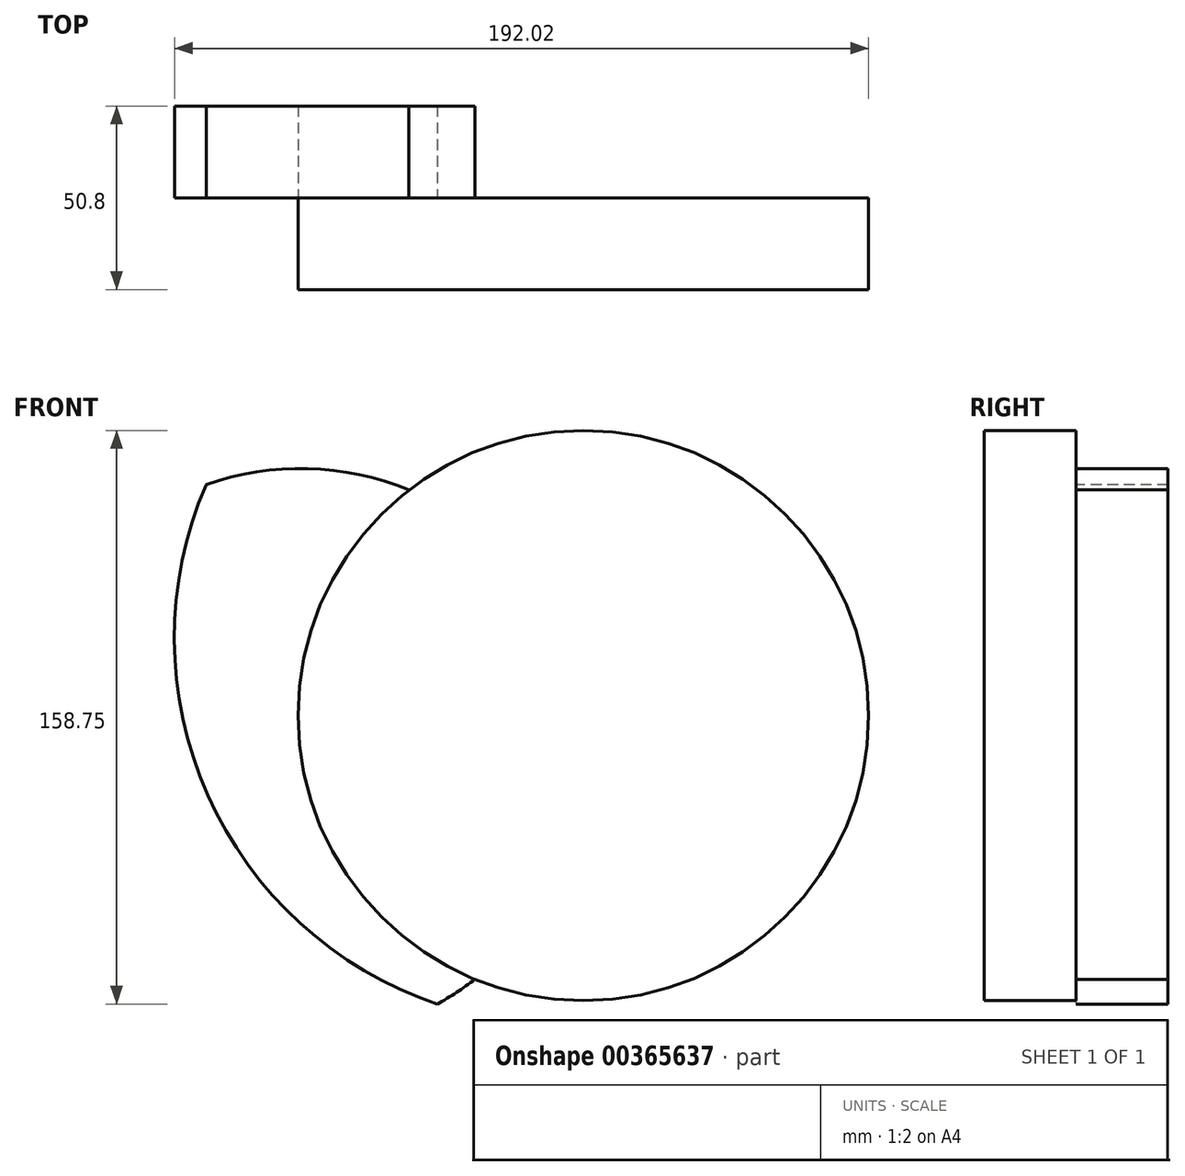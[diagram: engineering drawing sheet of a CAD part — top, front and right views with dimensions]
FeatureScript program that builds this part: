
annotation { "Feature Type Name" : "Feature", "Feature Type Description" : "" }
export const myFeature = defineFeature(function(context is Context, id is Id, definition is map)
    precondition{}
    {
        {
            var Q0;
            Q0=qCreatedBy(makeId("Front.planeOp"),FACE);
            var sketch = newSketch(context, id + "F0", { "sketchPlane" : qUnion([Q0])});
            skCircle(sketch, "E0", {"center": v(0, 0) * mm, "radius": 78.92 * mm});
            skSolve(sketch);
        }
        {
            var Q0;
            Q0=makeQuery(id+"F0.imprint","IMPRINT",FACE,{"disambiguationData":[TD([[makeQuery(id+"F0.imprint","IMPRINT",EDGE,{"derivedFrom":sQuery(id+"F0.wireOp",EDGE,"E0")}),1.0]])]});
            extrude(context, id + "F1", {"entities" : qUnion([Q0]), "depth" : 25.4 * mm});
        }
        {
            var Q0;
            Q0=makeQuery(id+"F1.opExtrude","CAP_FACE",FACE,{"disambiguationData":[OSD([sQuery(id+"F0.wireOp",EDGE,"E0")])],"isStart":true});
            var sketch = newSketch(context, id + "F2", { "sketchPlane" : qUnion([Q0])});
            skCircle(sketch, "E1", {"center": v(78.21, -10.54) * mm, "radius": 78.92 * mm});
            skCircle(sketch, "E2", {"center": v(6.1, 21.52) * mm, "radius": 107 * mm});
            skSolve(sketch);
        }
        {
            var Q0;
            {var subQ0=sQuery(id+"F2.wireOp",EDGE,"E1");var subQ1=makeQuery(id+"F1.opExtrude","CAP_EDGE",EDGE,{"disambiguationData":[OSD([sQuery(id+"F0.wireOp",EDGE,"E0")])],"isStart":true});var subQ2=makeQuery(id+"F2.imprint","INTERSECT",VERTEX,{"disambiguationData":[OD(0.0)],"derivedFrom":[subQ1,subQ0]});Q0=makeQuery(id+"F2.imprint","IMPRINT",FACE,{"disambiguationData":[TD([[makeQuery(id+"F2.imprint","IMPRINT",EDGE,{"disambiguationData":[TD([[subQ2,-1.0]])],"derivedFrom":subQ0}),1.0]])]});}
            var Q1;
            {var subQ0=sQuery(id+"F2.wireOp",EDGE,"E2");var subQ1=sQuery(id+"F2.wireOp",EDGE,"E1");var subQ2=makeQuery(id+"F2.imprint","INTERSECT",VERTEX,{"disambiguationData":[OD(0.0)],"derivedFrom":[subQ1,subQ0]});Q1=makeQuery(id+"F2.imprint","IMPRINT",FACE,{"disambiguationData":[TD([[makeQuery(id+"F2.imprint","IMPRINT",EDGE,{"disambiguationData":[TD([[subQ2,-1.0]])],"derivedFrom":subQ1}),-1.0]])]});}
            extrude(context, id + "F3", {"entities" : qUnion([Q0, Q1]), "operationType" : NewBodyOperationType.ADD, "depth" : 25.4 * mm});
        }
    });
